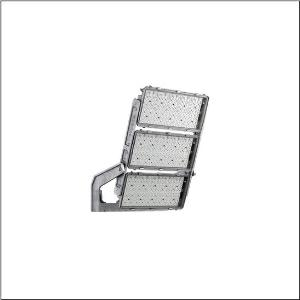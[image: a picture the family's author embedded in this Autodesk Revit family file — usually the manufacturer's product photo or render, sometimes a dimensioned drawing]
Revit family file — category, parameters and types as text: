
# Revit family: floodlight_fl_11_maxi_pro_remote___pl43_5xa779524a01ba_c92a
name_source: partatom
category: Lighting Fixtures
units: mm (PartAtom-declared; Revit-internal decimal feet)

## family parameters
Cut with Voids When Loaded = No
Host = Face
Light Source = No
Part Type = Normal
Room Calculation Point = No
Round Connector Dimension = Use Diameter
Shared = No

## types (1)
- --- (1 x LED, 108940 lm, 1020.5 W, 5700K)
    Apparent Load = 1020 VA
    CIE Flux Codes = 25 74 99 100 100
    Color Rendering = 90
    Color Temperature = 5700K
    Default Elevation = 1800 mm
    Description = Floodlight FL 11  maxi  pro Remote floodlight; light control with lens of PMMA; cover panel of toughened safety glass, transparent; light distribution: PL43, asymmetric direct distribution, LEDcolour temperature: 5700K, rated luminous flux: 108.940lm, colour rendering: CRI > 90, light colour: 957; luminous efficacy: 107lm/W; brightness control: DMX+RDM; with terminal, 8-pole, max. 2.5mm², mains connection: 220..240V/380..400V AC, 50/60Hz, surge voltage resistance: line to ground: 10kV, ECG replaceable separately, LED unit replaceable without ESD environment, dustproof LED module, dimming range 10..100%; 1021W floodlight with 3x LED unit of diecast aluminium, coated grey; length: 713mm / width: 651mm / height: 338mm; mounting bracket, of diecast aluminium, uncoated, natural, equipment: Longlife, protection rating (complete): IP66; insulation class (complete): insulation class I (protective earthing); certification: CE, ENEC, VDE; ball protection: ball impact resistance with accessories, impact resistance: IK07; only for outdoor installations, rated ambient temperature 10°C, permissible operating ambient temperature: -40..+40°C, permissible storage temperature: -40..+85°C; packaging unit: 1 piece

Light Distribution: PL43
    Height = 320 mm
    Lamp = 1 x LED
    Lamp Light Flux = 108940 lm
    Lamp Power = 1020.5 W
    Lamp count = 1
    Length = 1002 mm
    Luminous efficacy = 107 lm/W
    Manufacturer = Siteco
    ModVariant = No
    Model = 5XA779524A01BA
    Mounting Place = Ceiling
    Mounting Type = Surface mounted
    Number of Poles = 1
    OnlyDefault = Yes
    Power Factor = 1
    Product Name = Floodlight FL 11 maxi pro Remote | PL43
    Product group = floodlight | ceiling mounted
    ProductGroupID = 303
    Protection Class = Protection class I
    Protection Degree = IP 66
    RLX_Detail_Level = 1
    RLX_Emergency_Light_Flux = 0 lm
    RLX_Emergency_Type = 0
    RLX_Emergency_Type_DB = No
    RlxData = <blob elided: 52181 chars, md5=97836d81>
    Socket = socket
    Standby Power = 0 W
    System Light Flux = 108940 lm
    System Power = 1020 W
    Type Comments = factory setting: luminous flux: 100 % | dim-lin: 255 | 710 mA
    Type Image = l_1006784.jpg
    URL = http://relux.com
    VarID = @adj_045173
    Voltage = 0 V
    Weight = 0.00 kg
    Width = 655 mm

## geometry (parser evidence)
native form markers: Blend x4, Sweep x12
no freeform markers — native parametric forms only
